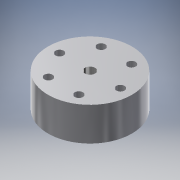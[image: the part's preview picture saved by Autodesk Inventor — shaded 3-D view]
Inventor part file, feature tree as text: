
AUTODESK INVENTOR PART (.ipt)
format: ipt  version: 2019.2 (Build 232265000, 265)  size: 545,280 bytes
history: native  units: mm
features: other x6, extrude x5, sketch x3, boolean_combine x1, plane x1, hole x1
ambient origin geometry x8: Origin, YZ Plane, XZ Plane, XY Plane, X Axis, Y Axis, Z Axis, Center Point
bodies: Solid1 (feature_tree), Solid3 (feature_tree)
feature tree (17):
  other  "MOT_WindowMotor_262100-3040.ipt"
  extrude  "Extrusion1"  Depth=30.0mm TaperAngle=0.0deg
  boolean_combine  "Combine2"
  other  "Thicken adapter hole"
  extrude  "Extrusion2"  Depth=0.225mm
  extrude  "Extrusion for middle hole"  Depth=4.5mm
  other  "Thicken Center Hole"
  extrude  "Extrusion for bolt holes"  Depth=2.0mm TaperAngle=0.0deg
  extrude  "Extrusion10"  Depth=4.5mm TaperAngle=0.0deg
  plane  "Work Plane1"
  sketch  "Sketch1"  dims[d0=70.0mm d1=30.0mm d2=0.0mm]
  other  "Solid1::MOT_WindowMotor_262100-3040.ipt"
  other  "TaggingFeature2"
  other  "Smooth Base"
  hole  "Hole to view fit"  [1 undecoded]
  sketch  "Sketch14"  dims[d7=10.0mm d8=0.225mm d9=0.5mm]
  sketch  "Sketch for bolt holes"  dims[d10=70.0mm d11=20.0mm d12=2.0mm d13=0.0mm d22=3.0mm d23=0.0mm d44=0.2mm d45=0.01mm d66=6.858mm d67=25.4mm d68=60.0mm d70=360.0deg d72=30.0mm d73=0.0mm d74=11.3665mm d75=60.0mm d77=360.0deg d79=4.5mm d80=0.0mm d81=35.0mm]
note: 1 required parameter value undecoded (feature->parameter linkage not recoverable at this tier; creation-order binding heuristic only, values carry confidence <= 0.55)
